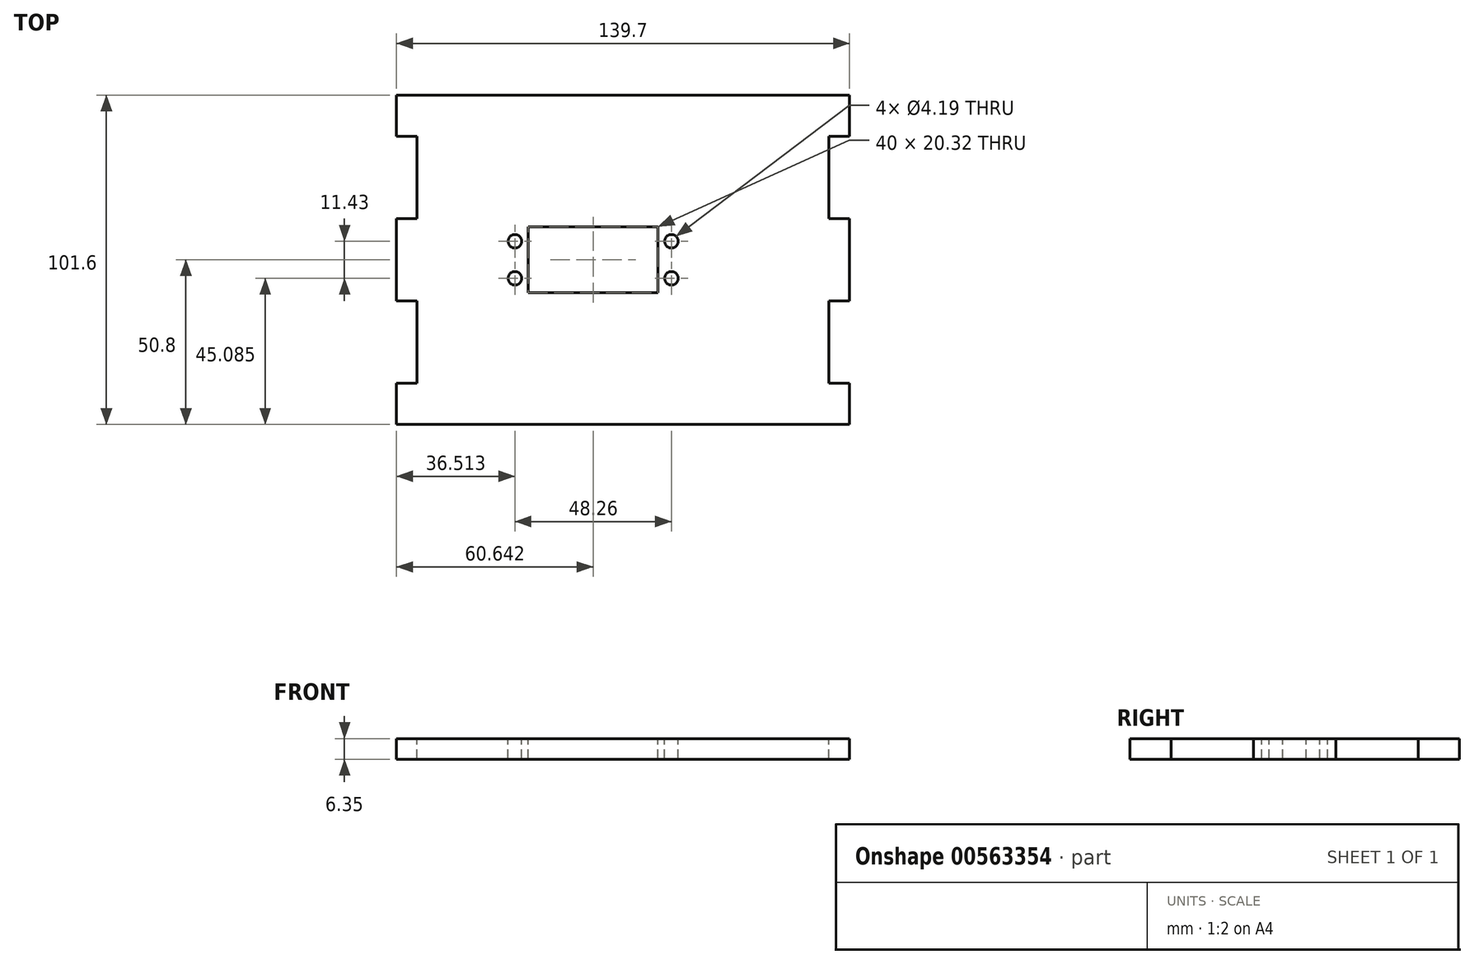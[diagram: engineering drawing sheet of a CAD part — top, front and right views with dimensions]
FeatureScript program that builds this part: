
annotation { "Feature Type Name" : "Feature", "Feature Type Description" : "" }
export const myFeature = defineFeature(function(context is Context, id is Id, definition is map)
    precondition{}
    {
        {
            var Q0;
            Q0=qCreatedBy(makeId("Top.planeOp"),FACE);
            var sketch = newSketch(context, id + "F0", { "sketchPlane" : qUnion([Q0])});
            skLineSegment(sketch, "E0.bottom", {"start": v(0, 0) * mm, "end": v(139.7, 0) * mm});
            skLineSegment(sketch, "E0.top", {"start": v(0, -101.6) * mm, "end": v(139.7, -101.6) * mm});
            skLineSegment(sketch, "E0.left", {"start": v(0, 0) * mm, "end": v(0, -101.6) * mm});
            skLineSegment(sketch, "E0.right", {"start": v(139.7, 0) * mm, "end": v(139.7, -101.6) * mm});
            skSolve(sketch);
        }
        {
            var Q0;
            Q0=makeQuery(id+"F0.imprint","IMPRINT",FACE,{"disambiguationData":[TD([[makeQuery(id+"F0.imprint","IMPRINT",EDGE,{"derivedFrom":sQuery(id+"F0.wireOp",EDGE,"E0.bottom")}),-1.0]])]});
            extrude(context, id + "F1", {"entities" : qUnion([Q0]), "depth" : 6.35 * mm, "offsetDistance" : 25.4 * mm});
        }
        {
            var Q0;
            Q0=makeQuery(id+"F1.opExtrude","CAP_FACE",FACE,{"disambiguationData":[OSD([sQuery(id+"F0.wireOp",EDGE,"E0.bottom"),sQuery(id+"F0.wireOp",EDGE,"E0.top"),sQuery(id+"F0.wireOp",EDGE,"E0.left"),sQuery(id+"F0.wireOp",EDGE,"E0.right")])],"isStart":false});
            var sketch = newSketch(context, id + "F2", { "sketchPlane" : qUnion([Q0])});
            skLineSegment(sketch, "E1.bottom", {"start": v(40.64, -40.64) * mm, "end": v(80.64, -40.64) * mm});
            skLineSegment(sketch, "E1.top", {"start": v(40.64, -60.96) * mm, "end": v(80.64, -60.96) * mm});
            skLineSegment(sketch, "E1.left", {"start": v(40.64, -40.64) * mm, "end": v(40.64, -60.96) * mm});
            skLineSegment(sketch, "E1.right", {"start": v(80.65, -40.64) * mm, "end": v(80.65, -60.96) * mm});
            skLineSegment(sketch, "E2", {"start": v(40.64, -50.8) * mm, "end": v(80.64, -50.8) * mm});
            skLineSegment(sketch, "E3", {"start": v(69.85, 0) * mm, "end": v(69.85, -101.6) * mm});
            skSolve(sketch);
        }
        {
            var Q0;
            Q0 = qSketchRegion(id + "F2", true);
            extrude(context, id + "F3", {"entities" : qUnion([Q0]), "operationType" : NewBodyOperationType.REMOVE, "oppositeDirection" : true, "depth" : 25.4 * mm, "offsetDistance" : 25.4 * mm});
        }
        {
            var Q0;
            Q0=makeQuery(id+"F1.opExtrude","CAP_FACE",FACE,{"disambiguationData":[OSD([sQuery(id+"F0.wireOp",EDGE,"E0.bottom"),sQuery(id+"F0.wireOp",EDGE,"E0.top"),sQuery(id+"F0.wireOp",EDGE,"E0.left"),sQuery(id+"F0.wireOp",EDGE,"E0.right")])],"isStart":false});
            var sketch = newSketch(context, id + "F4", { "sketchPlane" : qUnion([Q0])});
            skSolve(sketch);
        }
        {
            var Q0;
            Q0=makeQuery(id+"F4.imprint","IMPRINT",FACE,{"disambiguationData":[TD([[makeQuery(id+"F4.imprint","IMPRINT",EDGE,{"derivedFrom":makeQuery(id+"F1.opExtrude","CAP_EDGE",EDGE,{"disambiguationData":[OSD([sQuery(id+"F0.wireOp",EDGE,"E0.bottom")])],"isStart":false})}),-1.0]])]});
            var sketch = newSketch(context, id + "F5", { "sketchPlane" : qUnion([Q0])});
            skCircle(sketch, "E4", {"center": v(84.77, -45.08) * mm, "radius": 2.1 * mm});
            skCircle(sketch, "E5.MirrorC", {"center": v(84.77, -56.52) * mm, "radius": 2.1 * mm});
            skCircle(sketch, "E6.MirrorC", {"center": v(36.51, -45.08) * mm, "radius": 2.1 * mm});
            skCircle(sketch, "E7.MirrorC", {"center": v(36.51, -56.52) * mm, "radius": 2.1 * mm});
            skSolve(sketch);
        }
        {
            var Q0;
            Q0 = qSketchRegion(id + "F5", true);
            extrude(context, id + "F6", {"entities" : qUnion([Q0]), "operationType" : NewBodyOperationType.REMOVE, "oppositeDirection" : true, "depth" : 25.4 * mm, "offsetDistance" : 25.4 * mm});
        }
        {
            var Q0;
            Q0=makeQuery(id+"F4.imprint","IMPRINT",FACE,{"disambiguationData":[TD([[makeQuery(id+"F4.imprint","IMPRINT",EDGE,{"derivedFrom":makeQuery(id+"F1.opExtrude","CAP_EDGE",EDGE,{"disambiguationData":[OSD([sQuery(id+"F0.wireOp",EDGE,"E0.bottom")])],"isStart":false})}),-1.0]])]});
            var sketch = newSketch(context, id + "F7", { "sketchPlane" : qUnion([Q0])});
            skLineSegment(sketch, "E8.bottom", {"start": v(0, -12.7) * mm, "end": v(6.35, -12.7) * mm});
            skLineSegment(sketch, "E8.top", {"start": v(0, -38.1) * mm, "end": v(6.35, -38.1) * mm});
            skLineSegment(sketch, "E8.left", {"start": v(0, -12.7) * mm, "end": v(0, -38.1) * mm});
            skLineSegment(sketch, "E8.right", {"start": v(6.35, -12.7) * mm, "end": v(6.35, -38.1) * mm});
            skLineSegment(sketch, "E9", {"start": v(69.85, 0) * mm, "end": v(69.85, -114.3) * mm});
            skLineSegment(sketch, "E10", {"start": v(0, -50.8) * mm, "end": v(140.04, -50.8) * mm});
            skLineSegment(sketch, "E11.MirrorCS", {"start": v(6.35, -88.9) * mm, "end": v(6.35, -63.5) * mm});
            skLineSegment(sketch, "E12.MirrorCS", {"start": v(0, -63.5) * mm, "end": v(6.35, -63.5) * mm});
            skLineSegment(sketch, "E13.MirrorCS", {"start": v(0, -88.9) * mm, "end": v(0, -63.5) * mm});
            skLineSegment(sketch, "E14.MirrorCS", {"start": v(0, -88.9) * mm, "end": v(6.35, -88.9) * mm});
            skLineSegment(sketch, "E15.MirrorCS", {"start": v(139.7, -12.7) * mm, "end": v(139.7, -38.1) * mm});
            skLineSegment(sketch, "E16.MirrorCS", {"start": v(133.35, -12.7) * mm, "end": v(133.35, -38.1) * mm});
            skLineSegment(sketch, "E17.MirrorCS", {"start": v(139.7, -12.7) * mm, "end": v(133.35, -12.7) * mm});
            skLineSegment(sketch, "E18.MirrorCS", {"start": v(139.7, -38.1) * mm, "end": v(133.35, -38.1) * mm});
            skLineSegment(sketch, "E19.MirrorCS", {"start": v(139.7, -88.9) * mm, "end": v(133.35, -88.9) * mm});
            skLineSegment(sketch, "E20.MirrorCS", {"start": v(139.7, -63.5) * mm, "end": v(133.35, -63.5) * mm});
            skLineSegment(sketch, "E21.MirrorCS", {"start": v(139.7, -88.9) * mm, "end": v(139.7, -63.5) * mm});
            skLineSegment(sketch, "E22.MirrorCS", {"start": v(133.35, -88.9) * mm, "end": v(133.35, -63.5) * mm});
            skSolve(sketch);
        }
        {
            var Q0;
            Q0=makeQuery(id+"F7.imprint","IMPRINT",FACE,{"disambiguationData":[TD([[makeQuery(id+"F7.imprint","IMPRINT",EDGE,{"derivedFrom":sQuery(id+"F7.wireOp",EDGE,"E8.bottom")}),-1.0]])]});
            var Q1;
            Q1=makeQuery(id+"F7.imprint","IMPRINT",FACE,{"disambiguationData":[TD([[makeQuery(id+"F7.imprint","IMPRINT",EDGE,{"derivedFrom":sQuery(id+"F7.wireOp",EDGE,"E11.MirrorCS")}),1.0]])]});
            var Q2;
            Q2=makeQuery(id+"F7.imprint","IMPRINT",FACE,{"disambiguationData":[TD([[makeQuery(id+"F7.imprint","IMPRINT",EDGE,{"derivedFrom":sQuery(id+"F7.wireOp",EDGE,"E15.MirrorCS")}),-1.0]])]});
            var Q3;
            Q3=makeQuery(id+"F7.imprint","IMPRINT",FACE,{"disambiguationData":[TD([[makeQuery(id+"F7.imprint","IMPRINT",EDGE,{"derivedFrom":sQuery(id+"F7.wireOp",EDGE,"E19.MirrorCS")}),-1.0]])]});
            extrude(context, id + "F8", {"entities" : qUnion([Q0, Q1, Q2, Q3]), "operationType" : NewBodyOperationType.REMOVE, "oppositeDirection" : true, "depth" : 25.4 * mm, "offsetDistance" : 25.4 * mm});
        }
    });
